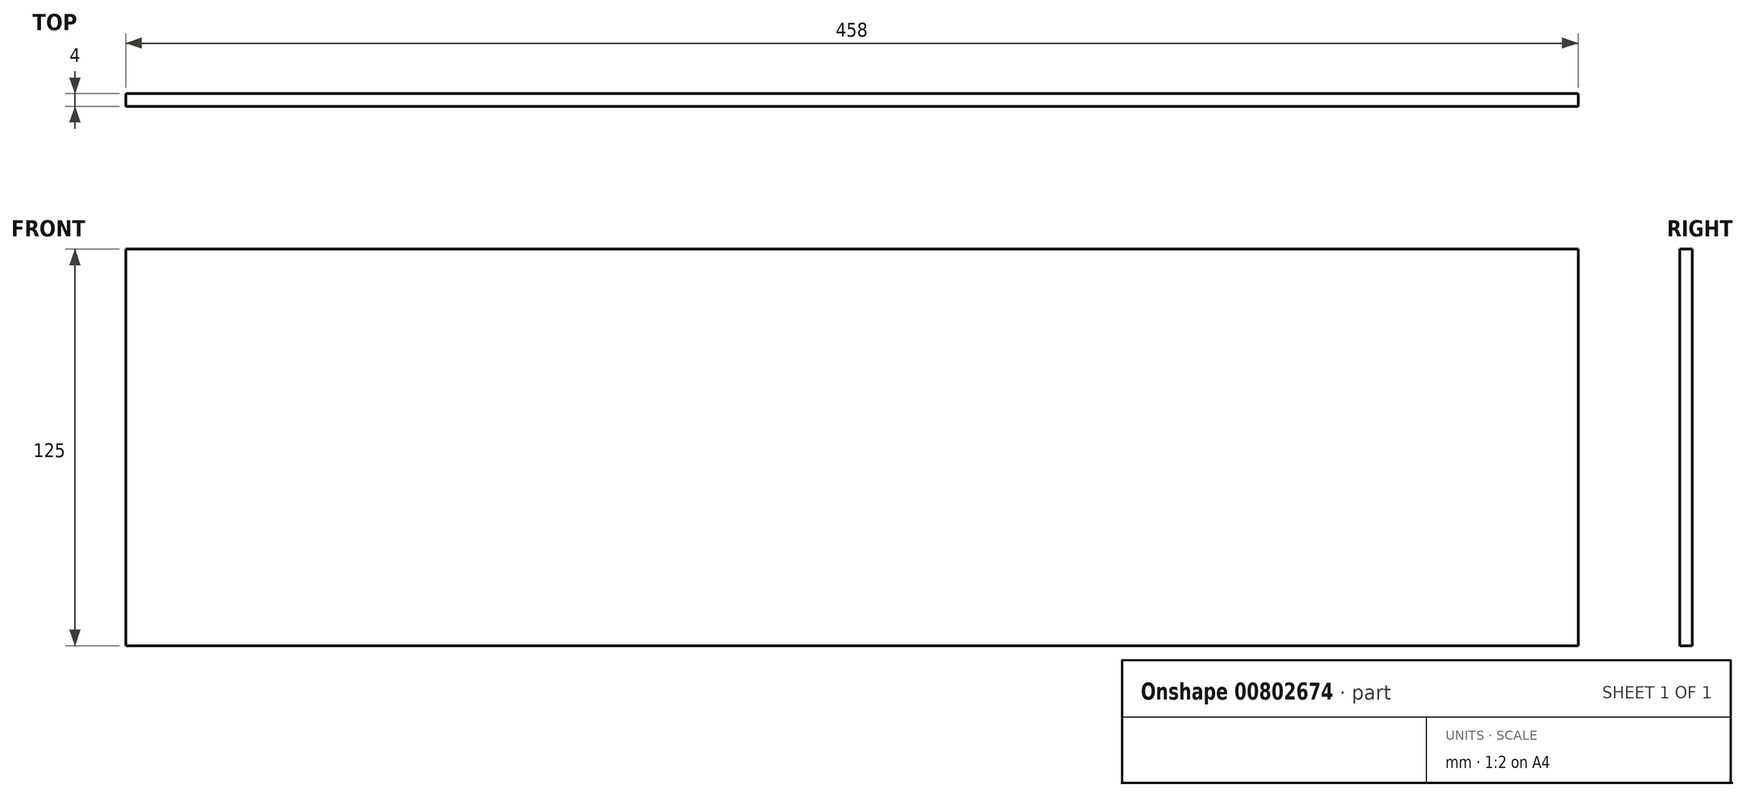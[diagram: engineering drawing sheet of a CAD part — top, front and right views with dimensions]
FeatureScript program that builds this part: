
annotation { "Feature Type Name" : "Feature", "Feature Type Description" : "" }
export const myFeature = defineFeature(function(context is Context, id is Id, definition is map)
    precondition{}
    {
        {
            var Q0;
            Q0=qCreatedBy(makeId("Front.planeOp"),FACE);
            var sketch = newSketch(context, id + "F0", { "sketchPlane" : qUnion([Q0])});
            skLineSegment(sketch, "E0.bottom", {"start": v(0, 0) * mm, "end": v(458, 0) * mm});
            skLineSegment(sketch, "E0.top", {"start": v(0, 125) * mm, "end": v(458, 125) * mm});
            skLineSegment(sketch, "E0.left", {"start": v(0, 0) * mm, "end": v(0, 125) * mm});
            skLineSegment(sketch, "E0.right", {"start": v(458, 0) * mm, "end": v(458, 125) * mm});
            skSolve(sketch);
        }
        {
            var Q0;
            Q0=makeQuery(id+"F0.imprint","IMPRINT",FACE,{"disambiguationData":[TD([[makeQuery(id+"F0.imprint","IMPRINT",EDGE,{"derivedFrom":sQuery(id+"F0.wireOp",EDGE,"E0.bottom")}),1.0]])]});
            extrude(context, id + "F1", {"entities" : qUnion([Q0]), "depth" : 4 * mm, "offsetDistance" : 25 * mm});
        }
    });
